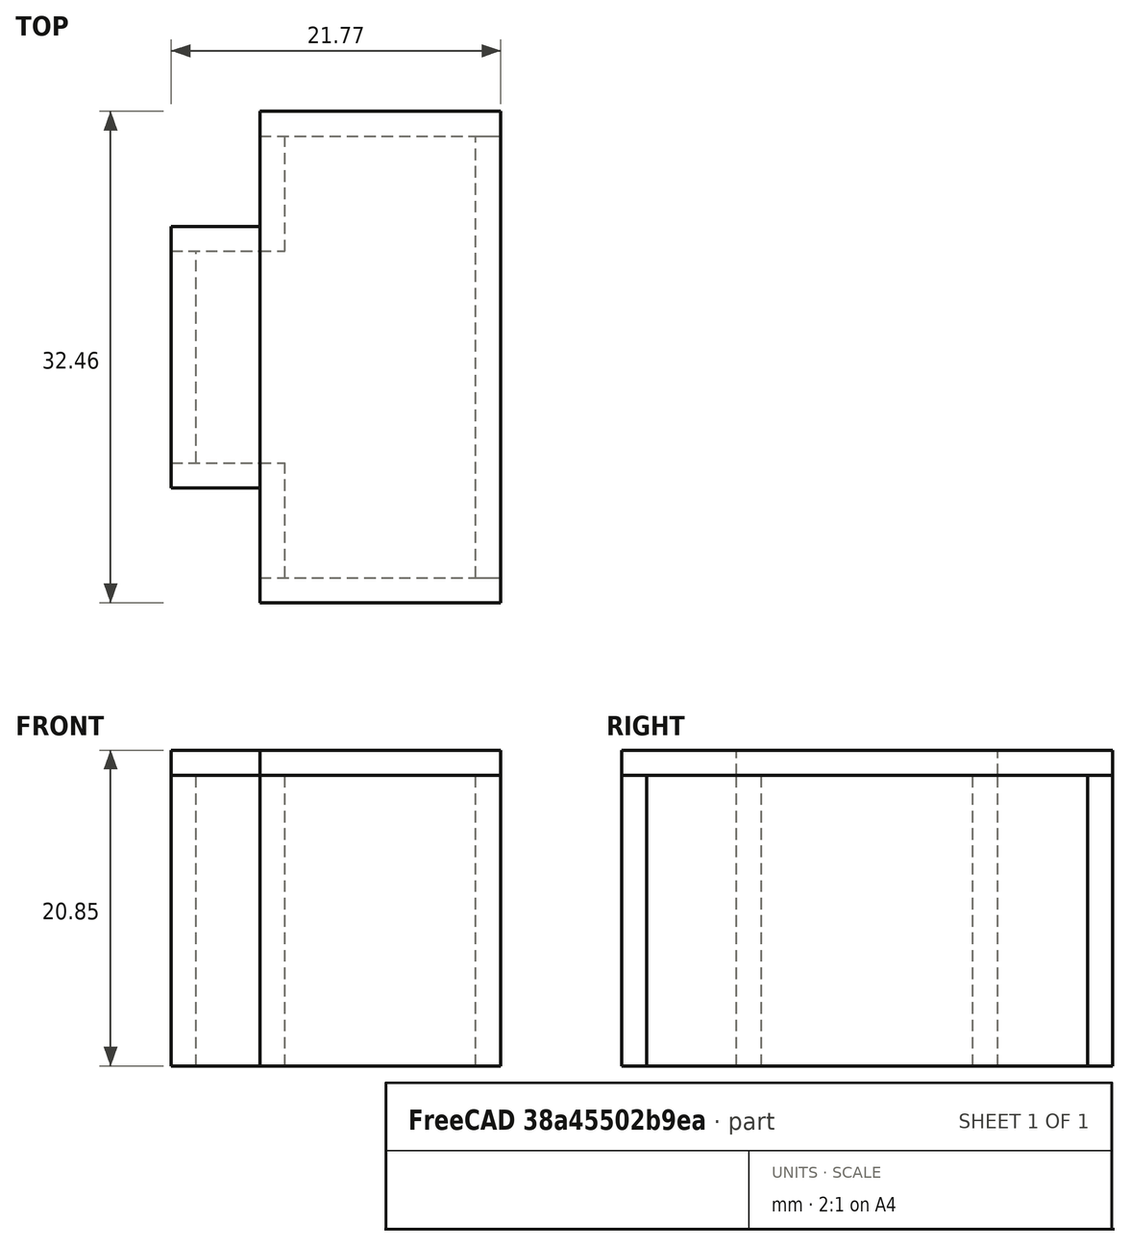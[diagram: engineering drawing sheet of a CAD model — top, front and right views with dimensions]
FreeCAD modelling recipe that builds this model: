
FCSTD DOCUMENT  (FreeCAD 0.18R16146 (Git))
Label: port1
License: All rights reserved
LicenseURL: http://en.wikipedia.org/wiki/All_rights_reserved
objects: Part::Box×10
note: 10 computed .brp shape members not serialized (recipe doc carries the construction recipe); baked Part::Feature solids carry a one-line shape summary decoded from their .brp

FEATURE [Part::Box] Box  label="Bottom"
  AttacherType = Attacher::AttachEngine3D
  Height = 19.2
  Length = 1.65
  Placement = pos=(-1.65,-14.58,0) rot=(0,0,1;0rad)
  Width = 29.16
FEATURE [Part::Box] Box001  label="Left1"
  AttacherType = Attacher::AttachEngine3D
  Height = 19.2
  Length = 15.91
  Placement = pos=(-15.91,14.58,0) rot=(0,0,1;0rad)
  Width = 1.65
FEATURE [Part::Box] Box002  label="Right1"
  AttacherType = Attacher::AttachEngine3D
  Height = 19.2
  Length = 15.91
  Placement = pos=(-15.91,-16.23,0) rot=(0,0,1;0rad)
  Width = 1.65
FEATURE [Part::Box] Box003  label="Left2"
  AttacherType = Attacher::AttachEngine3D
  Height = 19.2
  Length = 1.65
  Placement = pos=(-15.91,6.99,0) rot=(0,0,1;0rad)
  Width = 7.59
FEATURE [Part::Box] Box004  label="Right2"
  AttacherType = Attacher::AttachEngine3D
  Height = 19.2
  Length = 1.65
  Placement = pos=(-15.91,-14.58,0) rot=(0,0,1;0rad)
  Width = 7.59
FEATURE [Part::Box] Box005  label="Left3"
  AttacherType = Attacher::AttachEngine3D
  Height = 19.2
  Length = 5.86
  Placement = pos=(-21.77,6.99,0) rot=(0,0,1;0rad)
  Width = 1.65
FEATURE [Part::Box] Box006  label="Right3"
  AttacherType = Attacher::AttachEngine3D
  Height = 19.2
  Length = 5.86
  Placement = pos=(-21.77,-8.64,0) rot=(0,0,1;0rad)
  Width = 1.65
FEATURE [Part::Box] Box007  label="Top"
  AttacherType = Attacher::AttachEngine3D
  Height = 19.2
  Length = 1.65
  Placement = pos=(-21.77,-6.99,0) rot=(0,0,1;0rad)
  Width = 13.98
FEATURE [Part::Box] Box008  label="Back1"
  AttacherType = Attacher::AttachEngine3D
  Height = 1.65
  Length = 15.91
  Placement = pos=(-15.91,-16.23,19.2) rot=(0,0,1;0rad)
  Width = 32.46
FEATURE [Part::Box] Box009  label="Back2"
  AttacherType = Attacher::AttachEngine3D
  Height = 1.65
  Length = 5.86
  Placement = pos=(-21.77,-8.64,19.2) rot=(0,0,1;0rad)
  Width = 17.28
